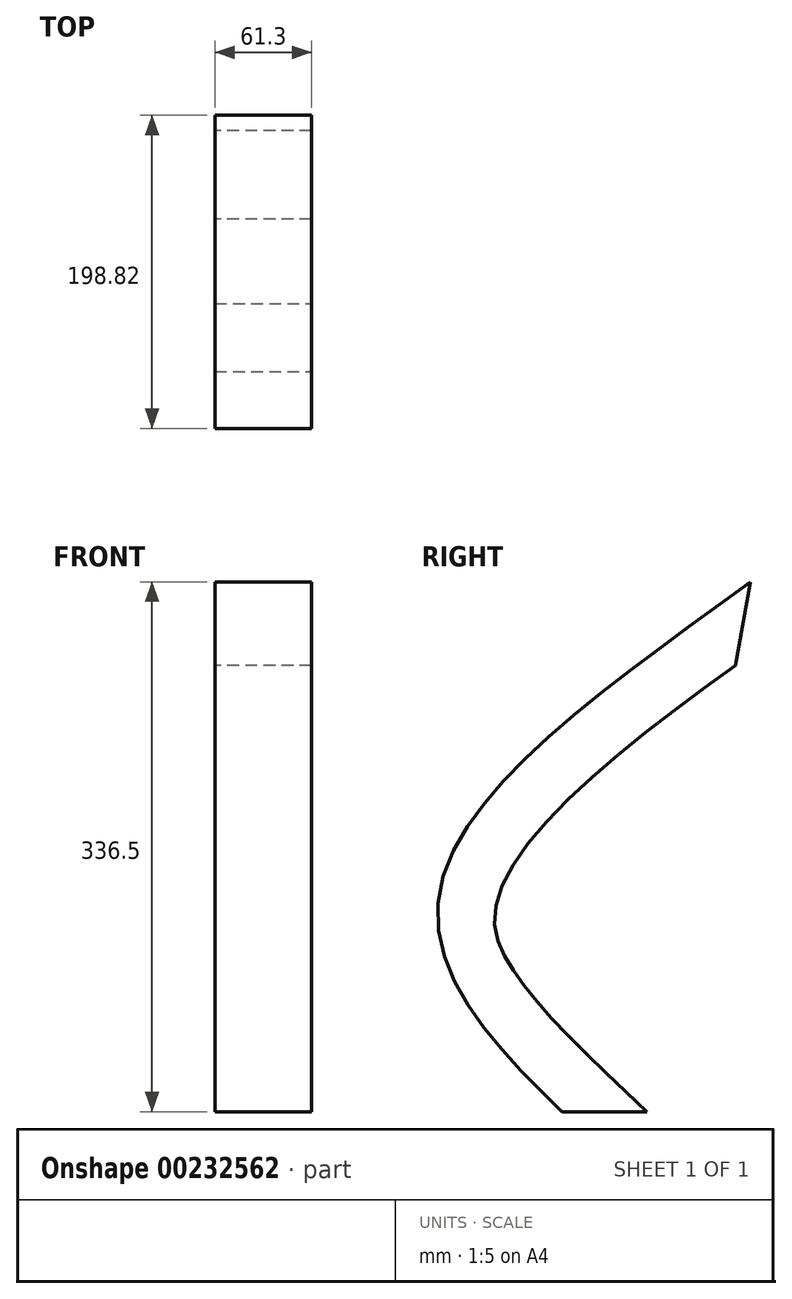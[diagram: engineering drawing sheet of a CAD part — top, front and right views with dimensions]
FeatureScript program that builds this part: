
annotation { "Feature Type Name" : "Feature", "Feature Type Description" : "" }
export const myFeature = defineFeature(function(context is Context, id is Id, definition is map)
    precondition{}
    {
        {
            var Q0;
            Q0=qCreatedBy(makeId("Top.planeOp"),FACE);
            var sketch = newSketch(context, id + "F0", { "sketchPlane" : qUnion([Q0])});
            skLineSegment(sketch, "E0", {"start": v(0, 0) * mm, "end": v(27.87, 0) * mm});
            skLineSegment(sketch, "E1", {"start": v(0, 0) * mm, "end": v(-33.43, 0) * mm});
            skLineSegment(sketch, "E2", {"start": v(27.87, 0) * mm, "end": v(27.87, 26.53) * mm});
            skLineSegment(sketch, "E3", {"start": v(27.87, 0) * mm, "end": v(27.87, -27.3) * mm});
            skLineSegment(sketch, "E4", {"start": v(-33.43, 0) * mm, "end": v(-33.43, 26.53) * mm});
            skLineSegment(sketch, "E5", {"start": v(-33.43, 0) * mm, "end": v(-33.43, -27.3) * mm});
            skLineSegment(sketch, "E6", {"start": v(27.87, 26.53) * mm, "end": v(-33.43, 26.53) * mm});
            skLineSegment(sketch, "E7", {"start": v(-33.43, -27.3) * mm, "end": v(27.87, -27.3) * mm});
            skSolve(sketch);
        }
        {
            var Q0;
            Q0=qCreatedBy(makeId("Right.planeOp"),FACE);
            var sketch = newSketch(context, id + "F1", { "sketchPlane" : qUnion([Q0])});
            skFitSpline(sketch, "E8", {"points": [v(0, 0) * mm, v(-85.16, 130.95) * mm, v(87.5, 309.63) * mm], "startDerivative": vector(-303.59, 290.74) * mm, "endDerivative": vector(449.59, 327.11) * mm});
            skSolve(sketch);
        }
        {
            var Q0;
            Q0=makeQuery(id+"F0.imprint","IMPRINT",FACE,{"disambiguationData":[TD([[makeQuery(id+"F0.imprint","IMPRINT",EDGE,{"derivedFrom":sQuery(id+"F0.wireOp",EDGE,"E0")}),1.0]])]});
            var Q1;
            Q1 = qConstructionFilter(qBodyType(qCreatedBy(id + "F1" ,EDGE), BodyType.WIRE), ConstructionObject.NO);
            sweep(context, id + "F2", {"profiles" : qUnion([Q0]), "path" : qUnion([Q1])});
        }
        {
            var Q0;
            Q0=makeQuery(id+"F0.imprint","IMPRINT",FACE,{"disambiguationData":[TD([[makeQuery(id+"F0.imprint","IMPRINT",EDGE,{"derivedFrom":sQuery(id+"F0.wireOp",EDGE,"E0")}),-1.0]])]});
            var Q1;
            Q1 = qConstructionFilter(qBodyType(qCreatedBy(id + "F1" ,EDGE), BodyType.WIRE), ConstructionObject.NO);
            sweep(context, id + "F3", {"operationType" : NewBodyOperationType.ADD, "profiles" : qUnion([Q0]), "path" : qUnion([Q1])});
        }
    });
